# Revit family: HVAC_HeatPumpAW_Enertech_CTC-EcoAir-400
name_source: partatom
category: Specialty Equipment
units: mm (PartAtom-declared; Revit-internal decimal feet)

## family parameters
Always vertical = Yes
Cut with Voids When Loaded = No
OmniClass Number = 23.75.00.00
OmniClass Title = Climate Control (HVAC)
Part Type = Normal
Room Calculation Point = No
Round Connector Dimension = Use Diameter
Shared = No
Work Plane-Based = No

## types (4) — shared parameters
AirFlow nominal (m3/h) = 0
AssetType = Fixed
BIMObjectName = HVAC_HeatPumpAW_Enertech_CTC-EcoAir-406
Brand = CTC
BrineSystem_Min_MaxPressure = 0-31
CO2Equivalent = 3.902
COP max: W35 & A -15 = 2.42
COP min: W35 & A +12 = 0
COP min: W35 & A +2 = 0
COP min: W35 & A +7 = 0
COP min: W35 & A -15 = 0
COP min: W35 & A -7 = 0
Capacity = Fixed
Category = Heat Pumps, Air-to-water
Color = Grey
CoolingCapacity min: A35 & W18 = 5000 W
Description = CTC EcoAir 400, a series of on/off air-to-water heat pumps available in six sizes with outputs of 6-17 kW. Model: 406-420
DurationUnit = Year
EER max: A35 & W18 = 0
EER max: A35 & W7 = 0
EER min: A35 & W18 = 0
EER min: A35 & W7 = 0
EER nominal: A35 & W18 = 0
EER nominal: A35 & W7 = 0
ElectricalDeviceNominalPower = 0 W
EnergyClassHeatingWithControl W35 = A++
EnergyClassHeatingWithControl W55 = A+
EnergyClassHeatingWithoutControl W35 = A++
EnergyClassHeatingWithoutControl W55 = A+
HasProtectiveEarth = Yes
IP_Code = IP X4
IfcExportAs = IfcElectricalDeviceCommon
IfcExportType = HEATER
InPutPower min: W35 & A +12 = 0 W
InPutPower min: W35 & A +2 = 0 W
InPutPower min: W35 & A +7 = 0 W
InPutPower min: W35 & A -15 = 0 W
InPutPower min: W35 & A -7 = 0 W
Manufacturer = CTC AB
ManufacturerCountry = Sweden
ManufacturerName = CTC AB
ManufacturerURL = https://ctc.se
Material = Steel
MaxOperatingPressureThermalStore = 3
NBSDescription = Air to water heat pumps
NBSReference = 90-40-40/320
Name = CTC-EcoAir-406
NominalCurrent = 0 A
NominalDepth = 545 mm
NominalFrequencyRange = 50 Hz
NominalHeight = 1080 mm  [stored 3.54331 ft]
NominalWidth = 1245 mm
PhaseAngle = 0.00°
PowerFactor = 0 W
ProductInformation = CTC EcoAir 400, a series of on/off air-to-water heat pumps available in six sizes with outputs of 6-17 kW. Model: 406-420
PumpMainMaterial = Steel - Grey
RatedHeatOutputCold Pdesigh W35 = 0 W
RatedHeatOutputCold Pdesigh W55 = 0 W
RatedHeatOutputModerate Pdesigh W35 = 0 W
RatedHeatOutputModerate Pdesigh W55 = 0 W
RatedHeatOutputWarm Pdesigh W35 = 0 W
RatedHeatOutputWarm Pdesigh W55 = 0 W
RefrigerantQuantity = 2.2
RefrigerantType = R407C
Revision = 6
SCOPCold W35 = 3.4
SCOPCold W55 = 2.7
SCOPModerate W35 = 3.9
SCOPModerate W55 = 3.0
Shape = Rectangular
Size = 545x1245x1080
SpecifiedOutput min: W35 & A +12 = 0 W
SpecifiedOutput min: W35 & A +2 = 0 W
SpecifiedOutput min: W35 & A +7 = 0 W
SpecifiedOutput min: W35 & A -15 = 0 W
SpecifiedOutput min: W35 & A -7 = 0 W
Touchscreen = no
UNSPSCCode = 40101806
URL = https://ctc-heating.com
Uniclass2 = Pr_40_70_65
Uniclass2015Description = Preparation catering equipment
Uniclass2015Reference = Pr_40_70_65
UsageCurrent = 0 A
Version = 6
VersionDate = 13/05/2024
WarrantyDurationUnit = Year
zero-valued in all types: Cost, Default Elevation

## per-type parameters (varying)
- CTC EcoAir 406 400V3N: AirFlow max (m3/h)=2500; COP max: W35 & A +12=5.44; COP max: W35 & A +2=3.66; COP max: W35 & A +7=4.78; COP max: W35 & A -7=3.1; CoolingCapacity max: A35 & W18=4000 W; CoolingCapacity max: A35 & W7=5000 W; CoolingCapacity min: A35 & W7=5000 W; CoolingCapacity nominal: A35 & W18=5000 W; CoolingCapacity nominal: A35 & W7=5000 W; EANNumber=7333077090111; GroupFuse=10; InPutPower max: W35 & A +12=1330 W; InPutPower max: W35 & A +2=1280 W; InPutPower max: W35 & A +7=1300 W; InPutPower max: W35 & A -15=1170 W; InPutPower max: W35 & A -7=1250 W; KvsValueProduct=5.1; MaxStartingCurrent=11.9; Model=CTC EcoAir 406; ModelNumber=585600001; NominalVoltage=400 V; NumberOfPoles=3; RatedCurrent=4 A; RatedVoltage=1200 V; SCOPWarm W35=4.8; SCOPWarm W55=3.6; Sound pressureLPA 10m=31; Sound pressureLPA 5m=37; SoundPowerLWA=56; SpecifiedOutput max: W35 & A +12=7240 W; SpecifiedOutput max: W35 & A +2=4690 W; SpecifiedOutput max: W35 & A +7=6220 W; SpecifiedOutput max: W35 & A -15=2840 W; SpecifiedOutput max: W35 & A -7=3870 W; WaterVolumeHeathingSystem=1.9; Weight=145
- CTC EcoAir 406 230V1N: AirFlow max (m3/h)=2500; COP max: W35 & A +12=5.44; COP max: W35 & A +2=3.66; COP max: W35 & A +7=4.78; COP max: W35 & A -7=3.1; CoolingCapacity max: A35 & W18=4000 W; CoolingCapacity max: A35 & W7=5000 W; CoolingCapacity min: A35 & W7=5000 W; CoolingCapacity nominal: A35 & W18=5000 W; CoolingCapacity nominal: A35 & W7=5000 W; EANNumber=7333077090166; GroupFuse=13; InPutPower max: W35 & A +12=1330 W; InPutPower max: W35 & A +2=1280 W; InPutPower max: W35 & A +7=1300 W; InPutPower max: W35 & A -15=1170 W; InPutPower max: W35 & A -7=1250 W; KvsValueProduct=5.1; MaxStartingCurrent=22.8; Model=CTC EcoAir 406; ModelNumber=585600011; NominalVoltage=230 V; NumberOfPoles=1; RatedCurrent=10 A; RatedVoltage=230 V; SCOPWarm W35=4.8; SCOPWarm W55=3.6; Sound pressureLPA 10m=31; Sound pressureLPA 5m=37; SoundPowerLWA=56; SpecifiedOutput max: W35 & A +12=7240 W; SpecifiedOutput max: W35 & A +2=4690 W; SpecifiedOutput max: W35 & A +7=6220 W; SpecifiedOutput max: W35 & A -15=2840 W; SpecifiedOutput max: W35 & A -7=3870 W; WaterVolumeHeathingSystem=1.9; Weight=145
- CTC EcoAir 408 400V3N: AirFlow max (m3/h)=2800; COP max: W35 & A +12=5.5; COP max: W35 & A +2=3.76; COP max: W35 & A +7=4.83; COP max: W35 & A -7=3.02; CoolingCapacity max: A35 & W18=7000 W; CoolingCapacity max: A35 & W7=6000 W; CoolingCapacity min: A35 & W7=6000 W; CoolingCapacity nominal: A35 & W18=6000 W; CoolingCapacity nominal: A35 & W7=6000 W; EANNumber=733077090128; GroupFuse=10; InPutPower max: W35 & A +12=1660 W; InPutPower max: W35 & A +2=1600 W; InPutPower max: W35 & A +7=1620 W; InPutPower max: W35 & A -15=1500 W; InPutPower max: W35 & A -7=1570 W; KvsValueProduct=6.5; MaxStartingCurrent=10.8; Model=CTC EcoAir 408; ModelNumber=585600002; NominalVoltage=400 V; NumberOfPoles=3; RatedCurrent=5 A; RatedVoltage=1200 V; SCOPWarm W35=4.9; SCOPWarm W55=3.8; Sound pressureLPA 10m=33; Sound pressureLPA 5m=39; SoundPowerLWA=58; SpecifiedOutput max: W35 & A +12=9120 W; SpecifiedOutput max: W35 & A +2=6020 W; SpecifiedOutput max: W35 & A +7=7830 W; SpecifiedOutput max: W35 & A -15=3630 W; SpecifiedOutput max: W35 & A -7=4730 W; WaterVolumeHeathingSystem=2.4; Weight=150
- CTC EcoAir 408 230V1N: AirFlow max (m3/h)=2800; COP max: W35 & A +12=5.5; COP max: W35 & A +2=3.76; COP max: W35 & A +7=4.83; COP max: W35 & A -7=3.02; CoolingCapacity max: A35 & W18=7000 W; CoolingCapacity max: A35 & W7=6000 W; CoolingCapacity min: A35 & W7=6000 W; CoolingCapacity nominal: A35 & W18=6000 W; CoolingCapacity nominal: A35 & W7=6000 W; EANNumber=7333077090173; GroupFuse=13; InPutPower max: W35 & A +12=1660 W; InPutPower max: W35 & A +2=1600 W; InPutPower max: W35 & A +7=1620 W; InPutPower max: W35 & A -15=1500 W; InPutPower max: W35 & A -7=1570 W; KvsValueProduct=6.5; MaxStartingCurrent=23.2; Model=CTC EcoAir 408; ModelNumber=585600012; NominalVoltage=230 V; NumberOfPoles=1; RatedCurrent=12 A; RatedVoltage=230 V; SCOPWarm W35=4.9; SCOPWarm W55=3.8; Sound pressureLPA 10m=33; Sound pressureLPA 5m=39; SoundPowerLWA=58; SpecifiedOutput max: W35 & A +12=9120 W; SpecifiedOutput max: W35 & A +2=6020 W; SpecifiedOutput max: W35 & A +7=7830 W; SpecifiedOutput max: W35 & A -15=3630 W; SpecifiedOutput max: W35 & A -7=4730 W; WaterVolumeHeathingSystem=2.4; Weight=150

note: [stored X ft] marks values corroborated as IEEE doubles in the binary element streams (Revit-internal decimal feet)

## geometry (parser evidence)
native form markers: Sweep x5
no freeform markers — native parametric forms only
